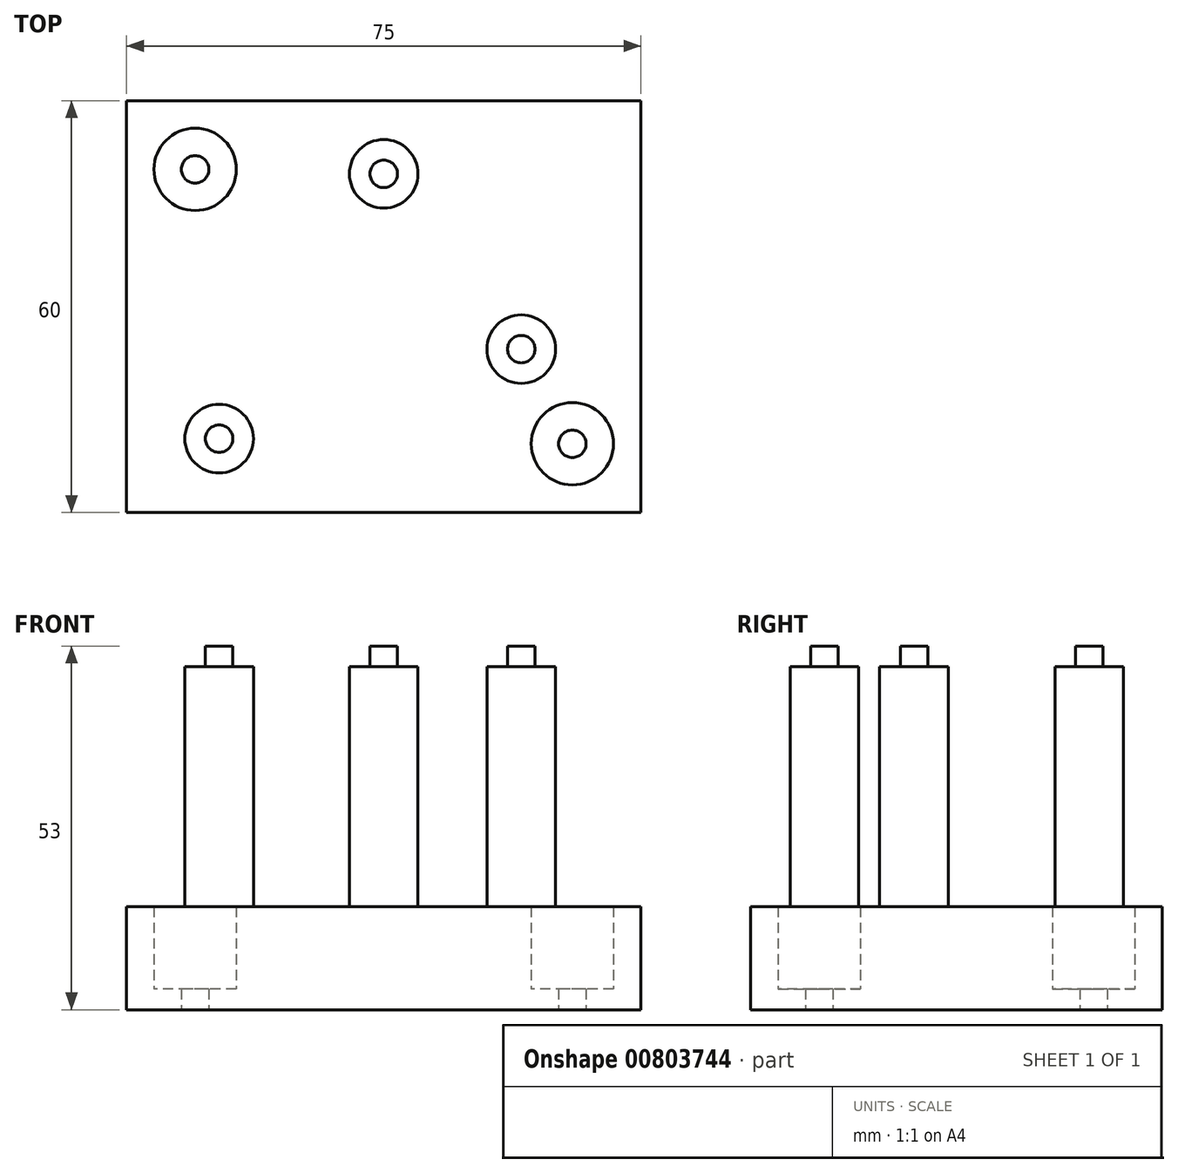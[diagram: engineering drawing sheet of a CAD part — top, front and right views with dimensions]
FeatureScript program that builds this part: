
annotation { "Feature Type Name" : "Feature", "Feature Type Description" : "" }
export const myFeature = defineFeature(function(context is Context, id is Id, definition is map)
    precondition{}
    {
        {
            var Q0;
            Q0=qCreatedBy(makeId("Top.planeOp"),FACE);
            var sketch = newSketch(context, id + "F0", { "sketchPlane" : qUnion([Q0])});
            skLineSegment(sketch, "E0.bottom", {"start": v(37.5, 30) * mm, "end": v(-37.5, 30) * mm});
            skLineSegment(sketch, "E0.top", {"start": v(37.5, -30) * mm, "end": v(-37.5, -30) * mm});
            skLineSegment(sketch, "E0.left", {"start": v(37.5, 30) * mm, "end": v(37.5, -30) * mm});
            skLineSegment(sketch, "E0.right", {"start": v(-37.5, 30) * mm, "end": v(-37.5, -30) * mm});
            skPoint(sketch, "E0.middle", {"position": v(0, 0) * mm});
            skLineSegment(sketch, "E1", {"start": v(0, 0) * mm, "end": v(0, 19.35) * mm});
            skLineSegment(sketch, "E2", {"start": v(0, 0) * mm, "end": v(20.05, 0) * mm});
            skLineSegment(sketch, "E3", {"start": v(20.05, 0) * mm, "end": v(20.05, -6.2) * mm});
            skLineSegment(sketch, "E4", {"start": v(0, 0) * mm, "end": v(-24, 0) * mm});
            skLineSegment(sketch, "E5", {"start": v(-24, 0) * mm, "end": v(-24, -19.25) * mm});
            skCircle(sketch, "E6", {"center": v(0, 19.35) * mm, "radius": 5 * mm});
            skCircle(sketch, "E7", {"center": v(0, 19.35) * mm, "radius": 2 * mm});
            skCircle(sketch, "E8", {"center": v(20.05, -6.2) * mm, "radius": 5 * mm});
            skCircle(sketch, "E9", {"center": v(20.05, -6.2) * mm, "radius": 2 * mm});
            skCircle(sketch, "E10", {"center": v(-24, -19.25) * mm, "radius": 5 * mm});
            skCircle(sketch, "E11", {"center": v(-24, -19.25) * mm, "radius": 2 * mm});
            skLineSegment(sketch, "E12.bottom", {"start": v(-37.5, 30) * mm, "end": v(-27.5, 30) * mm});
            skLineSegment(sketch, "E12.top", {"start": v(-37.5, 20) * mm, "end": v(-27.5, 20) * mm});
            skLineSegment(sketch, "E12.left", {"start": v(-37.5, 30) * mm, "end": v(-37.5, 20) * mm});
            skLineSegment(sketch, "E12.right", {"start": v(-27.5, 30) * mm, "end": v(-27.5, 20) * mm});
            skLineSegment(sketch, "E13.bottom", {"start": v(37.5, -30) * mm, "end": v(27.5, -30) * mm});
            skLineSegment(sketch, "E13.top", {"start": v(37.5, -20) * mm, "end": v(27.5, -20) * mm});
            skLineSegment(sketch, "E13.left", {"start": v(37.5, -30) * mm, "end": v(37.5, -20) * mm});
            skLineSegment(sketch, "E13.right", {"start": v(27.5, -30) * mm, "end": v(27.5, -20) * mm});
            skCircle(sketch, "E14", {"center": v(-27.5, 20) * mm, "radius": 6 * mm});
            skCircle(sketch, "E15", {"center": v(-27.5, 20) * mm, "radius": 2 * mm});
            skCircle(sketch, "E16", {"center": v(27.5, -20) * mm, "radius": 6 * mm});
            skCircle(sketch, "E17", {"center": v(27.5, -20) * mm, "radius": 2 * mm});
            skSolve(sketch);
        }
        {
            var Q0;
            Q0 = qSketchRegion(id + "F0", true);
            extrude(context, id + "F1", {"entities" : qUnion([Q0]), "depth" : 15 * mm, "offsetDistance" : 25 * mm});
        }
        {
            var Q0;
            {var subQ0=sQuery(id+"F0.wireOp",EDGE,"E14");var subQ1=sQuery(id+"F0.wireOp",EDGE,"E12.top");var subQ2=makeQuery(id+"F0.imprint","INTERSECT",VERTEX,{"derivedFrom":[subQ1,subQ0]});Q0=makeQuery(id+"F0.imprint","IMPRINT",FACE,{"disambiguationData":[TD([[makeQuery(id+"F0.imprint","IMPRINT",EDGE,{"disambiguationData":[TD([[subQ2,-1.0]])],"derivedFrom":subQ1}),-1.0]])]});}
            var Q1;
            {var subQ0=sQuery(id+"F0.wireOp",EDGE,"E14");var subQ1=sQuery(id+"F0.wireOp",EDGE,"E12.top");var subQ2=makeQuery(id+"F0.imprint","INTERSECT",VERTEX,{"derivedFrom":[subQ1,subQ0]});Q1=makeQuery(id+"F0.imprint","IMPRINT",FACE,{"disambiguationData":[TD([[makeQuery(id+"F0.imprint","IMPRINT",EDGE,{"disambiguationData":[TD([[subQ2,-1.0]])],"derivedFrom":subQ1}),1.0]])]});}
            var Q2;
            {var subQ0=sQuery(id+"F0.wireOp",EDGE,"E16");var subQ1=sQuery(id+"F0.wireOp",EDGE,"E13.top");var subQ2=makeQuery(id+"F0.imprint","INTERSECT",VERTEX,{"derivedFrom":[subQ1,subQ0]});Q2=makeQuery(id+"F0.imprint","IMPRINT",FACE,{"disambiguationData":[TD([[makeQuery(id+"F0.imprint","IMPRINT",EDGE,{"disambiguationData":[TD([[subQ2,-1.0]])],"derivedFrom":subQ1}),1.0]])]});}
            var Q3;
            {var subQ0=sQuery(id+"F0.wireOp",EDGE,"E16");var subQ1=sQuery(id+"F0.wireOp",EDGE,"E13.top");var subQ2=makeQuery(id+"F0.imprint","INTERSECT",VERTEX,{"derivedFrom":[subQ1,subQ0]});Q3=makeQuery(id+"F0.imprint","IMPRINT",FACE,{"disambiguationData":[TD([[makeQuery(id+"F0.imprint","IMPRINT",EDGE,{"disambiguationData":[TD([[subQ2,-1.0]])],"derivedFrom":subQ1}),-1.0]])]});}
            extrude(context, id + "F2", {"entities" : qUnion([Q0, Q1, Q2, Q3]), "operationType" : NewBodyOperationType.ADD, "depth" : 3 * mm, "offsetDistance" : 25 * mm});
        }
        {
            var Q0;
            Q0=makeQuery(id+"F0.imprint","IMPRINT",FACE,{"disambiguationData":[TD([[makeQuery(id+"F0.imprint","IMPRINT",EDGE,{"derivedFrom":sQuery(id+"F0.wireOp",EDGE,"E6")}),1.0]])]});
            var Q1;
            Q1=makeQuery(id+"F0.imprint","IMPRINT",FACE,{"disambiguationData":[TD([[makeQuery(id+"F0.imprint","IMPRINT",EDGE,{"derivedFrom":sQuery(id+"F0.wireOp",EDGE,"E10")}),1.0]])]});
            var Q2;
            Q2=makeQuery(id+"F0.imprint","IMPRINT",FACE,{"disambiguationData":[TD([[makeQuery(id+"F0.imprint","IMPRINT",EDGE,{"derivedFrom":sQuery(id+"F0.wireOp",EDGE,"E8")}),1.0]])]});
            extrude(context, id + "F3", {"entities" : qUnion([Q0, Q1, Q2]), "operationType" : NewBodyOperationType.ADD, "depth" : 50 * mm, "offsetDistance" : 25 * mm});
        }
        {
            var Q0;
            Q0=makeQuery(id+"F0.imprint","IMPRINT",FACE,{"disambiguationData":[TD([[makeQuery(id+"F0.imprint","IMPRINT",EDGE,{"derivedFrom":sQuery(id+"F0.wireOp",EDGE,"E7")}),1.0]])]});
            var Q1;
            Q1=makeQuery(id+"F0.imprint","IMPRINT",FACE,{"disambiguationData":[TD([[makeQuery(id+"F0.imprint","IMPRINT",EDGE,{"derivedFrom":sQuery(id+"F0.wireOp",EDGE,"E11")}),1.0]])]});
            var Q2;
            Q2=makeQuery(id+"F0.imprint","IMPRINT",FACE,{"disambiguationData":[TD([[makeQuery(id+"F0.imprint","IMPRINT",EDGE,{"derivedFrom":sQuery(id+"F0.wireOp",EDGE,"E9")}),1.0]])]});
            extrude(context, id + "F4", {"entities" : qUnion([Q0, Q1, Q2]), "operationType" : NewBodyOperationType.ADD, "depth" : 53 * mm, "offsetDistance" : 25 * mm});
        }
    });
